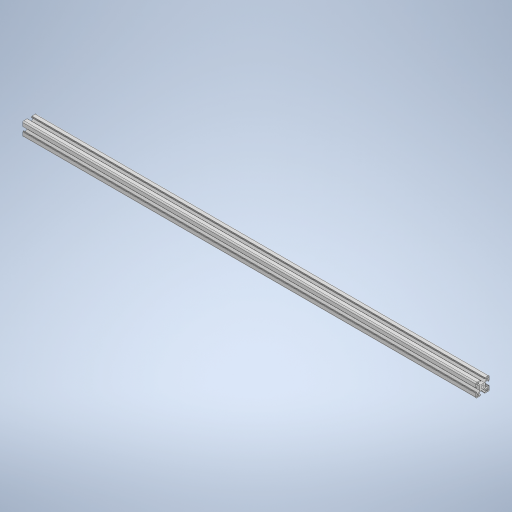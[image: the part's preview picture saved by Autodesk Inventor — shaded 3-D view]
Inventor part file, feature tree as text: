
AUTODESK INVENTOR PART (.ipt)
format: ipt  version: 2023 (Build 270158000, 158)  size: 374,272 bytes
history: native  units: mm
features: extrude x1, mirror x1, pattern_circular x1, sketch x1
ambient origin geometry x8: Origin, YZ Plane, XZ Plane, XY Plane, X Axis, Y Axis, Z Axis, Center Point
bodies: Solid1 (feature_tree)
feature tree (4):
  extrude  "Extrusion1"  TaperAngle=45.0deg  [1 undecoded]
  mirror  "Mirror1"
  pattern_circular  "Circular Pattern1"  Angle=45.0deg  [1 undecoded]
  sketch  "Sketch1"  dims[d0=3.4mm d1=45.0deg d3=45.0deg d4=2.5mm d5=135.0deg d6=1.0mm d7=4.1mm d8=5.2mm d9=8.25mm d10=15.0mm d11=2.2mm d12=5.8mm d13=1.5mm d14=1.5mm d15=1.0mm d16=1.0mm d17=1.0mm d18=1000.0mm d19=0.0mm d20=40.0mm d21=360.0deg]
note: 2 required parameter values undecoded (feature->parameter linkage not recoverable at this tier; creation-order binding heuristic only, values carry confidence <= 0.55)
